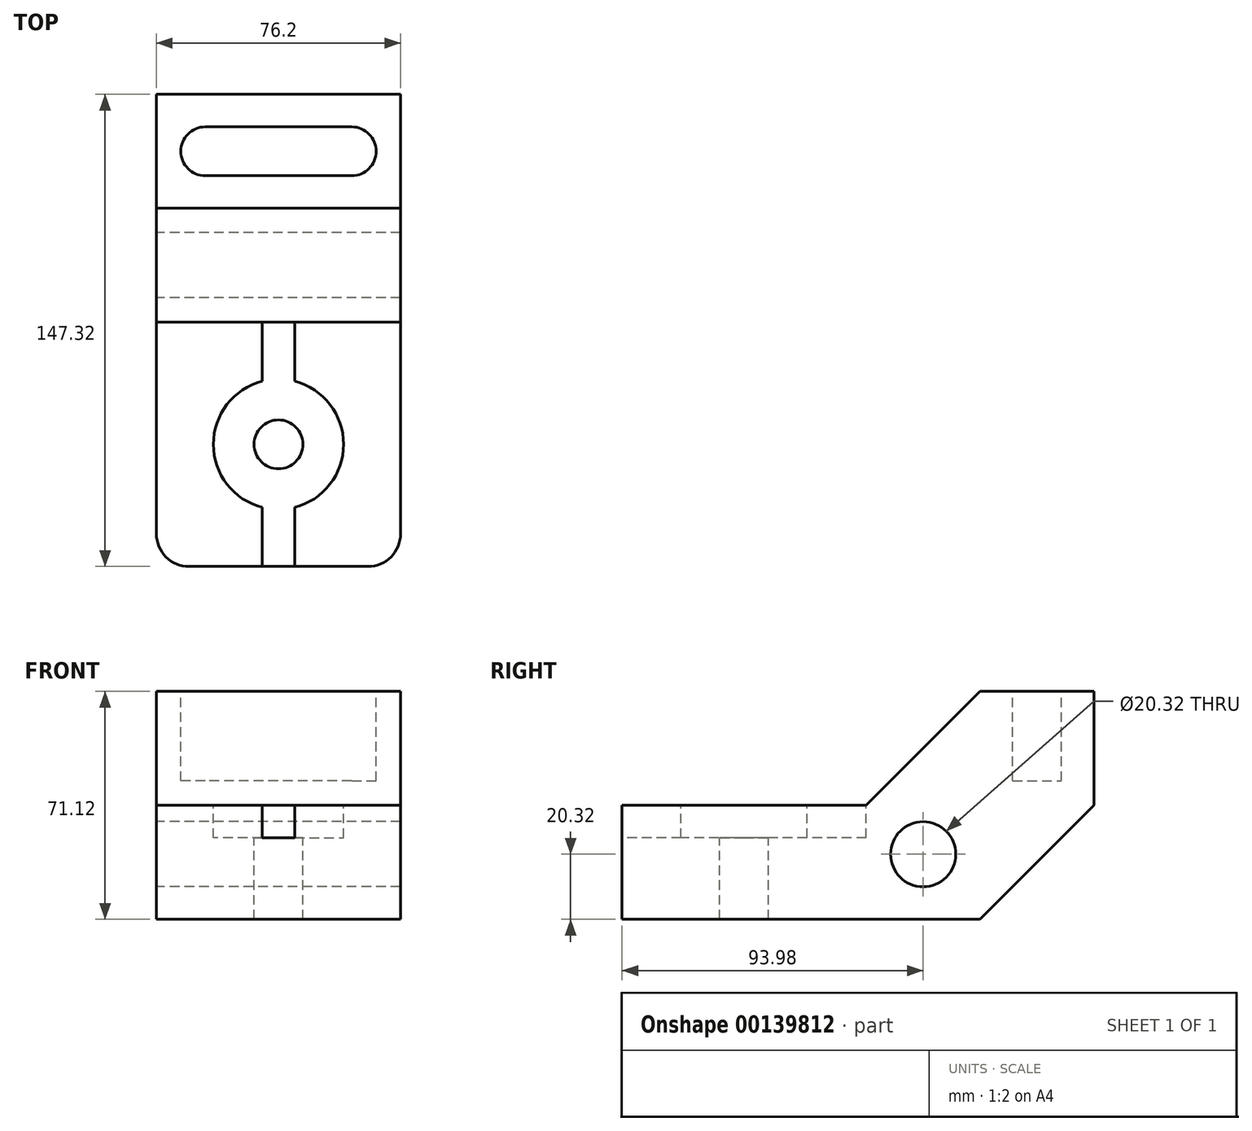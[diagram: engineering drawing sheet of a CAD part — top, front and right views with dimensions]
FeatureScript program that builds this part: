
annotation { "Feature Type Name" : "Feature", "Feature Type Description" : "" }
export const myFeature = defineFeature(function(context is Context, id is Id, definition is map)
    precondition{}
    {
        {
            var Q0;
            Q0=qCreatedBy(makeId("Right.planeOp"),FACE);
            var sketch = newSketch(context, id + "F0", { "sketchPlane" : qUnion([Q0])});
            skLineSegment(sketch, "E0", {"start": v(0, 0) * mm, "end": v(-76.2, 0) * mm});
            skLineSegment(sketch, "E1", {"start": v(-76.2, 0) * mm, "end": v(-76.2, -35.56) * mm});
            skLineSegment(sketch, "E2", {"start": v(-76.2, -35.56) * mm, "end": v(35.56, -35.56) * mm});
            skLineSegment(sketch, "E3", {"start": v(35.56, -35.56) * mm, "end": v(71.12, 0) * mm});
            skLineSegment(sketch, "E4", {"start": v(71.12, 0) * mm, "end": v(71.12, 35.56) * mm});
            skLineSegment(sketch, "E5", {"start": v(71.12, 35.56) * mm, "end": v(35.56, 35.56) * mm});
            skLineSegment(sketch, "E6", {"start": v(35.56, 35.56) * mm, "end": v(0, 0) * mm});
            skLineSegment(sketch, "E7", {"start": v(71.12, 0) * mm, "end": v(17.78, 0) * mm, "construction": true});
            skLineSegment(sketch, "E8", {"start": v(17.78, 0) * mm, "end": v(17.78, -15.24) * mm, "construction": true});
            skCircle(sketch, "E9", {"center": v(17.78, -15.24) * mm, "radius": 10.16 * mm});
            skSolve(sketch);
        }
        {
            var Q0;
            Q0 = qSketchRegion(id + "F0", true);
            extrude(context, id + "F1", {"entities" : qUnion([Q0]), "endBound" : BoundingType.SYMMETRIC, "depth" : 76.2 * mm});
        }
        {
            var Q0;
            Q0=makeQuery(id+"F1.opExtrude","SWEPT_FACE",FACE,{"disambiguationData":[OSD([sQuery(id+"F0.wireOp",EDGE,"E5")])]});
            var sketch = newSketch(context, id + "F2", { "sketchPlane" : qUnion([Q0])});
            skLineSegment(sketch, "E10", {"start": v(-38.1, 53.34) * mm, "end": v(-22.86, 53.34) * mm, "construction": true});
            skLineSegment(sketch, "E11", {"start": v(-22.86, 53.34) * mm, "end": v(22.86, 53.34) * mm, "construction": true});
            skArc(sketch, "E12", {"start": v(-22.86, 60.96) * mm, "mid": v(-30.48, 53.34) * mm, "end": v(-22.86, 45.72) * mm});
            skArc(sketch, "E13", {"start": v(22.86, 45.72) * mm, "mid": v(30.48, 53.34) * mm, "end": v(22.86, 60.96) * mm});
            skLineSegment(sketch, "E14", {"start": v(22.86, 60.96) * mm, "end": v(-22.86, 60.96) * mm});
            skLineSegment(sketch, "E15", {"start": v(22.86, 45.72) * mm, "end": v(-22.86, 45.72) * mm});
            skSolve(sketch);
        }
        {
            var Q0;
            Q0 = qSketchRegion(id + "F2", true);
            extrude(context, id + "F3", {"entities" : qUnion([Q0]), "operationType" : NewBodyOperationType.REMOVE, "oppositeDirection" : true, "depth" : 27.94 * mm});
        }
        {
            var Q0;
            Q0=makeQuery(id+"F1.opExtrude","SWEPT_FACE",FACE,{"disambiguationData":[OSD([sQuery(id+"F0.wireOp",EDGE,"E0")])]});
            var sketch = newSketch(context, id + "F4", { "sketchPlane" : qUnion([Q0])});
            skLineSegment(sketch, "E16", {"start": v(0, -76.2) * mm, "end": v(0, -38.1) * mm, "construction": true});
            skSolve(sketch);
        }
        {
            var Q0;
            Q0=sQuery(id+"F4.wireOp",VERTEX,"E16.end");
            var Q1;
            Q1=makeQuery(id+"F1.opExtrude","SWEPT_BODY",BODY,{"disambiguationData":[OSD([sQuery(id+"F0.wireOp",EDGE,"E0"),sQuery(id+"F0.wireOp",EDGE,"E1"),sQuery(id+"F0.wireOp",EDGE,"E2"),sQuery(id+"F0.wireOp",EDGE,"E3"),sQuery(id+"F0.wireOp",EDGE,"E4"),sQuery(id+"F0.wireOp",EDGE,"E5"),sQuery(id+"F0.wireOp",EDGE,"E6"),sQuery(id+"F0.wireOp",EDGE,"E9")])]});
            hole(context, id + "F5", {"style" : HoleStyle.C_BORE, "endStyle" : HoleEndStyle.THROUGH, "holeDiameter" : 15.24 * mm, "cBoreDiameter" : 40.64 * mm, "cBoreDepth" : 10.16 * mm, "locations" : qUnion([Q0]), "scope" : qUnion([Q1]), "isTappedThrough" : true});
        }
        {
            var Q0;
            Q0=makeQuery(id+"F1.opExtrude","SWEPT_FACE",FACE,{"disambiguationData":[OSD([sQuery(id+"F0.wireOp",EDGE,"E1")])]});
            var sketch = newSketch(context, id + "F6", { "sketchPlane" : qUnion([Q0])});
            skLineSegment(sketch, "E17.bottom", {"start": v(5.08, -10.16) * mm, "end": v(-5.08, -10.16) * mm});
            skLineSegment(sketch, "E17.top", {"start": v(5.08, 10.16) * mm, "end": v(-5.08, 10.16) * mm});
            skLineSegment(sketch, "E17.left", {"start": v(5.08, -10.16) * mm, "end": v(5.08, 10.16) * mm});
            skLineSegment(sketch, "E17.right", {"start": v(-5.08, -10.16) * mm, "end": v(-5.08, 10.16) * mm});
            skPoint(sketch, "E17.middle", {"position": v(0, 0) * mm});
            skSolve(sketch);
        }
        {
            var Q0;
            Q0 = qSketchRegion(id + "F6", true);
            extrude(context, id + "F7", {"entities" : qUnion([Q0]), "operationType" : NewBodyOperationType.REMOVE, "oppositeDirection" : true, "depth" : 76.2 * mm});
        }
        {
            var Q0;
            Q0=makeQuery(id+"F1.opExtrude","CAP_EDGE",EDGE,{"disambiguationData":[OSD([sQuery(id+"F0.wireOp",EDGE,"E1")])],"isStart":true});
            var Q1;
            Q1=makeQuery(id+"F1.opExtrude","CAP_EDGE",EDGE,{"disambiguationData":[OSD([sQuery(id+"F0.wireOp",EDGE,"E1")])],"isStart":false});
            fillet(context, id + "F8", {"entities" : qUnion([Q0, Q1]), "radius" : 10.16 * mm, "tangentPropagation" : true, "allowEdgeOverflow" : false});
        }
    });
